# Revit family: Drain_Floor_Ligature_Resistant_Zurn-Z400LRS
name_source: partatom
category: Plumbing Fixtures
units: mm (PartAtom-declared; Revit-internal decimal feet)

## family parameters
Always vertical = Yes
Cut with Voids When Loaded = No
Maintain Annotation Orientation = No
OmniClass Number = 23.70.00.00
OmniClass Title = Waste Management
Part Type = Normal
Room Calculation Point = No
Round Connector Dimension = Use Radius
Shared = No
Work Plane-Based = No

## types (4) — shared parameters
Assembly Code = D2030300
Description = TYPE LRS SQUARE LIGATURE RESISTANT STRAINER TOP
Manufacturer = Zurn Water, LLC
Manufacurer Brand = Zurn
Model = Z400LRS
Product Documentation Link = https://files.zurn.com
Product Page URL = https://www.zurn.com
Product data url = https://www.bimobject.com
URL = www.zurn.com
zero-valued in all types: Approx. Weight (Lbs), Default Elevation

## per-type parameters (varying)
| type | Half_Width | Height | Main Material | Width |
| ZN400-5LRS | 2.5 " | 2 " | Nickel Bronze - Zurn Industries LLC - Polished | 5 " |
| ZN400-6LRS | 3 " | 2.25 " | Nickel Bronze - Zurn Industries LLC - Polished | 6 " |
| ZS400-5LRS | 2.5 " | 2 " | Steel - Zurn - Stainless 304 | 5 " |
| ZS400-6LRS | 3 " | 2.25 " | Steel - Zurn - Stainless 304 | 6 " |

note: column(s) folded — value = type name in every type: Type Comments

## geometry (parser evidence)
native form markers: Sweep x2
no freeform markers — native parametric forms only
